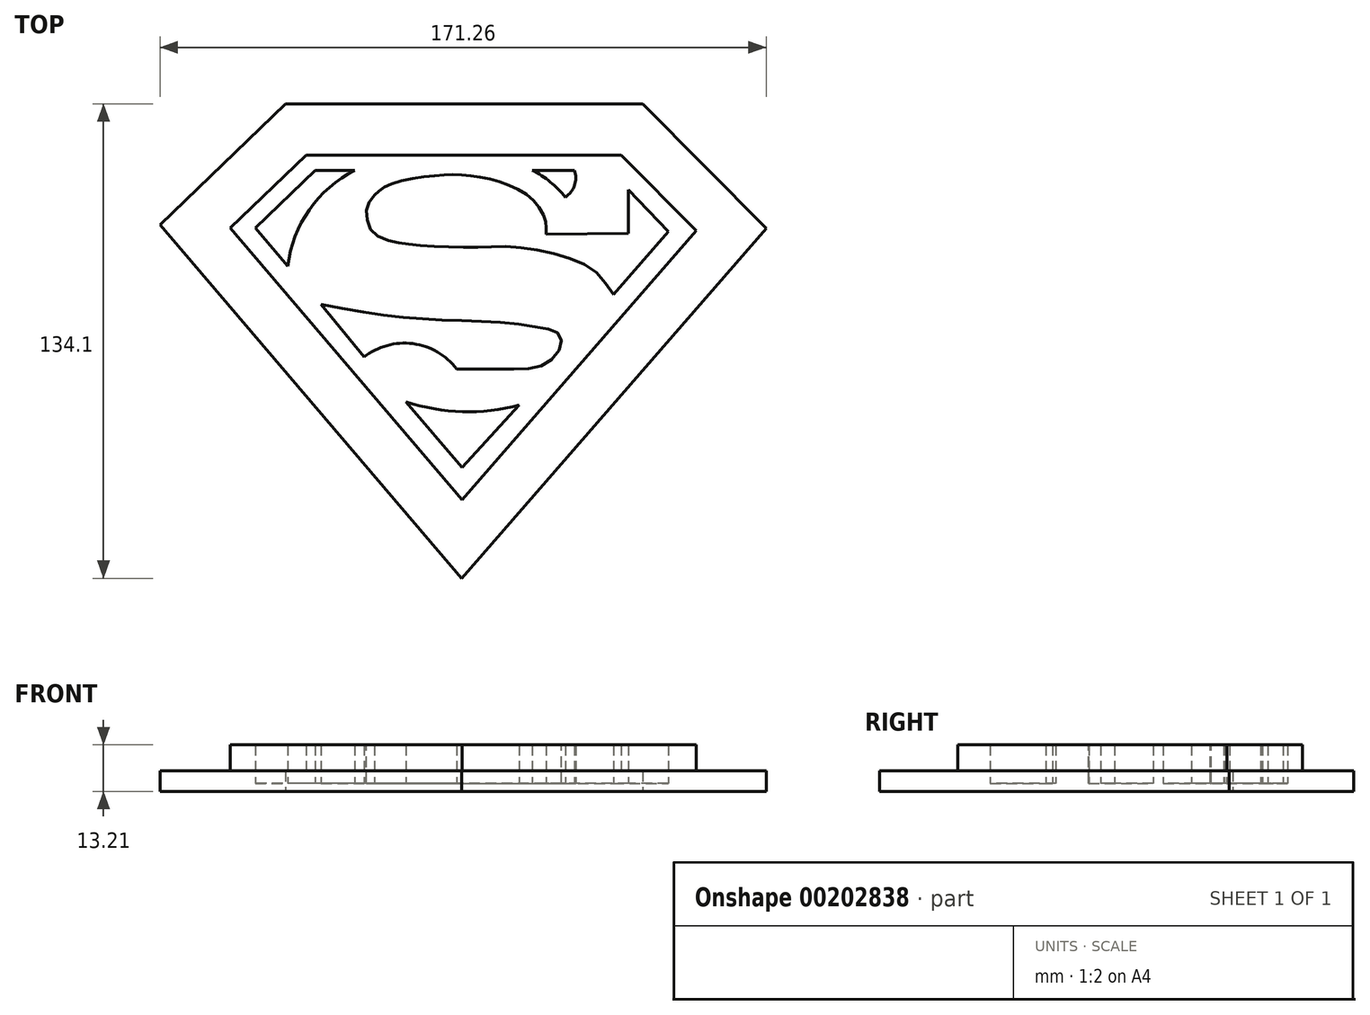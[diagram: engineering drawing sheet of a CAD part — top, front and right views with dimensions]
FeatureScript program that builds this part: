
annotation { "Feature Type Name" : "Feature", "Feature Type Description" : "" }
export const myFeature = defineFeature(function(context is Context, id is Id, definition is map)
    precondition{}
    {
        {
            var Q0;
            Q0=qCreatedBy(makeId("Top.planeOp"),FACE);
            var sketch = newSketch(context, id + "F0", { "sketchPlane" : qUnion([Q0])});
            skLineSegment(sketch, "E0", {"start": v(-53.74, 31.7) * mm, "end": v(11.72, -45.1) * mm});
            skLineSegment(sketch, "E1", {"start": v(11.72, -45.1) * mm, "end": v(77.91, 30.96) * mm});
            skLineSegment(sketch, "E2", {"start": v(77.91, 30.96) * mm, "end": v(56.72, 52.34) * mm});
            skLineSegment(sketch, "E3", {"start": v(56.72, 52.34) * mm, "end": v(-32.36, 52.34) * mm});
            skLineSegment(sketch, "E4", {"start": v(-32.36, 52.34) * mm, "end": v(-53.74, 31.7) * mm});
            skLineSegment(sketch, "E5", {"start": v(-18.6, 48.07) * mm, "end": v(-29.75, 48.07) * mm});
            skLineSegment(sketch, "E6", {"start": v(-29.75, 48.07) * mm, "end": v(-46.7, 31.7) * mm});
            skLineSegment(sketch, "E7", {"start": v(-46.7, 31.7) * mm, "end": v(-37.53, 20.94) * mm});
            skArc(sketch, "E8", {"start": v(-18.6, 48.07) * mm, "mid": v(-31.45, 36.87) * mm, "end": v(-37.53, 20.94) * mm});
            skFitSpline(sketch, "E9", {"points": [v(-13.02, 41) * mm, v(-9.3, 43.8) * mm, v(2.6, 46.4) * mm, v(11.72, 46.77) * mm, v(21.38, 45.1) * mm, v(30.68, 40.63) * mm, v(35.15, 34.3) * mm, v(35.52, 30.03) * mm], "startDerivative": vector(26.77, 27.4) * mm, "endDerivative": vector(-1.55, -39.26) * mm});
            skFitSpline(sketch, "E10", {"points": [v(-13.02, 41) * mm, v(-15.06, 38.03) * mm, v(-15.06, 33.93) * mm, v(-13.02, 30.03) * mm, v(-7.44, 27.8) * mm, v(-2.6, 27.05) * mm, v(5.76, 26.5) * mm, v(15.8, 26.31) * mm, v(25.1, 26.5) * mm, v(37.75, 24.45) * mm, v(48.72, 19.99) * mm, v(54.48, 12.92) * mm], "startDerivative": vector(-39.18, -43.26) * mm, "endDerivative": vector(48.35, -76.59) * mm});
            skLineSegment(sketch, "E11", {"start": v(54.48, 12.92) * mm, "end": v(70.01, 30.76) * mm});
            skLineSegment(sketch, "E12", {"start": v(70.01, 30.76) * mm, "end": v(58.76, 42.49) * mm});
            skLineSegment(sketch, "E13", {"start": v(58.76, 42.49) * mm, "end": v(58.76, 30.22) * mm});
            skLineSegment(sketch, "E14", {"start": v(58.76, 30.22) * mm, "end": v(35.52, 30.03) * mm});
            skLineSegment(sketch, "E15", {"start": v(-28.08, 10.13) * mm, "end": v(-16, -4.74) * mm});
            skArc(sketch, "E16", {"start": v(10.23, -8.1) * mm, "mid": v(-2.18, -0.94) * mm, "end": v(-16, -4.74) * mm});
            skPoint(sketch, "E17.3.internal.snap0", {"position": v(-21.01, -6.7) * mm});
            skFitSpline(sketch, "E17", {"points": [v(10.23, -8.1) * mm, v(16.55, -8.1) * mm, v(28.08, -8.1) * mm, v(35.33, -6.7) * mm, v(39.42, -2.14) * mm, v(39.24, 1.58) * mm, v(35.52, 3.25) * mm, v(24.36, 4.93) * mm, v(7.81, 5.67) * mm, v(-8.93, 6.97) * mm, v(-28.08, 10.13) * mm], "startDerivative": vector(70.37, 0.36) * mm, "endDerivative": vector(-137.16, 25.14) * mm});
            skArc(sketch, "E18", {"start": v(-4.1, -17.39) * mm, "mid": v(11.83, -20.17) * mm, "end": v(27.9, -18.32) * mm});
            skLineSegment(sketch, "E19", {"start": v(-4.1, -17.39) * mm, "end": v(11.75, -35.98) * mm});
            skLineSegment(sketch, "E20", {"start": v(11.75, -35.98) * mm, "end": v(27.9, -18.32) * mm});
            skLineSegment(sketch, "E21", {"start": v(31.61, 48.07) * mm, "end": v(43.51, 48.07) * mm});
            skArc(sketch, "E22", {"start": v(40.9, 40.44) * mm, "mid": v(43.52, 43.8) * mm, "end": v(43.51, 48.07) * mm});
            skArc(sketch, "E23", {"start": v(40.9, 40.44) * mm, "mid": v(36.66, 44.75) * mm, "end": v(31.61, 48.07) * mm});
            skSolve(sketch);
        }
        {
            var Q0;
            Q0=makeQuery(id+"F0.imprint","IMPRINT",FACE,{"disambiguationData":[TD([[makeQuery(id+"F0.imprint","IMPRINT",EDGE,{"derivedFrom":sQuery(id+"F0.wireOp",EDGE,"E0")}),1.0]])]});
            extrude(context, id + "F1", {"entities" : qUnion([Q0]), "depth" : 13.2 * mm});
        }
        {
            var Q0;
            Q0=qCreatedBy(makeId("Top.planeOp"),FACE);
            var sketch = newSketch(context, id + "F2", { "sketchPlane" : qUnion([Q0])});
            skLineSegment(sketch, "E24.0", {"start": v(-53.74, 31.7) * mm, "end": v(11.72, -45.1) * mm});
            skLineSegment(sketch, "E25.0", {"start": v(11.72, -45.1) * mm, "end": v(77.91, 30.96) * mm});
            skLineSegment(sketch, "E26.0", {"start": v(77.91, 30.96) * mm, "end": v(56.72, 52.34) * mm});
            skLineSegment(sketch, "E27.0", {"start": v(56.72, 52.34) * mm, "end": v(-32.36, 52.34) * mm});
            skLineSegment(sketch, "E28.0", {"start": v(-32.36, 52.34) * mm, "end": v(-53.74, 31.7) * mm});
            skLineSegment(sketch, "E29.0", {"start": v(11.6, -67.28) * mm, "end": v(97.67, 31.6) * mm});
            skLineSegment(sketch, "E29.1", {"start": v(-73.59, 32.67) * mm, "end": v(11.6, -67.28) * mm});
            skLineSegment(sketch, "E29.2", {"start": v(97.67, 31.6) * mm, "end": v(62.75, 66.82) * mm});
            skLineSegment(sketch, "E29.3", {"start": v(62.75, 66.82) * mm, "end": v(-38.2, 66.82) * mm});
            skLineSegment(sketch, "E29.4", {"start": v(-38.2, 66.82) * mm, "end": v(-73.59, 32.67) * mm});
            skSolve(sketch);
        }
        {
            var Q0;
            Q0=makeQuery(id+"F2.imprint","IMPRINT",FACE,{"disambiguationData":[TD([[makeQuery(id+"F2.imprint","IMPRINT",EDGE,{"derivedFrom":sQuery(id+"F2.wireOp",EDGE,"E24.0")}),-1.0]])]});
            extrude(context, id + "F3", {"entities" : qUnion([Q0]), "operationType" : NewBodyOperationType.ADD, "depth" : 5.84 * mm});
        }
        {
            var Q0;
            Q0=makeQuery(id+"F0.imprint","IMPRINT",FACE,{"disambiguationData":[TD([[makeQuery(id+"F0.imprint","IMPRINT",EDGE,{"derivedFrom":sQuery(id+"F0.wireOp",EDGE,"E9")}),-1.0]])]});
            var Q1;
            Q1=makeQuery(id+"F0.imprint","IMPRINT",FACE,{"disambiguationData":[TD([[makeQuery(id+"F0.imprint","IMPRINT",EDGE,{"derivedFrom":sQuery(id+"F0.wireOp",EDGE,"E5")}),1.0]])]});
            var Q2;
            Q2=makeQuery(id+"F0.imprint","IMPRINT",FACE,{"disambiguationData":[TD([[makeQuery(id+"F0.imprint","IMPRINT",EDGE,{"derivedFrom":sQuery(id+"F0.wireOp",EDGE,"E21")}),-1.0]])]});
            var Q3;
            Q3=makeQuery(id+"F0.imprint","IMPRINT",FACE,{"disambiguationData":[TD([[makeQuery(id+"F0.imprint","IMPRINT",EDGE,{"derivedFrom":sQuery(id+"F0.wireOp",EDGE,"E15")}),1.0]])]});
            var Q4;
            Q4=makeQuery(id+"F0.imprint","IMPRINT",FACE,{"disambiguationData":[TD([[makeQuery(id+"F0.imprint","IMPRINT",EDGE,{"derivedFrom":sQuery(id+"F0.wireOp",EDGE,"E18")}),-1.0]])]});
            extrude(context, id + "F4", {"entities" : qUnion([Q0, Q1, Q2, Q3, Q4]), "operationType" : NewBodyOperationType.ADD, "depth" : 2.3 * mm});
        }
    });
